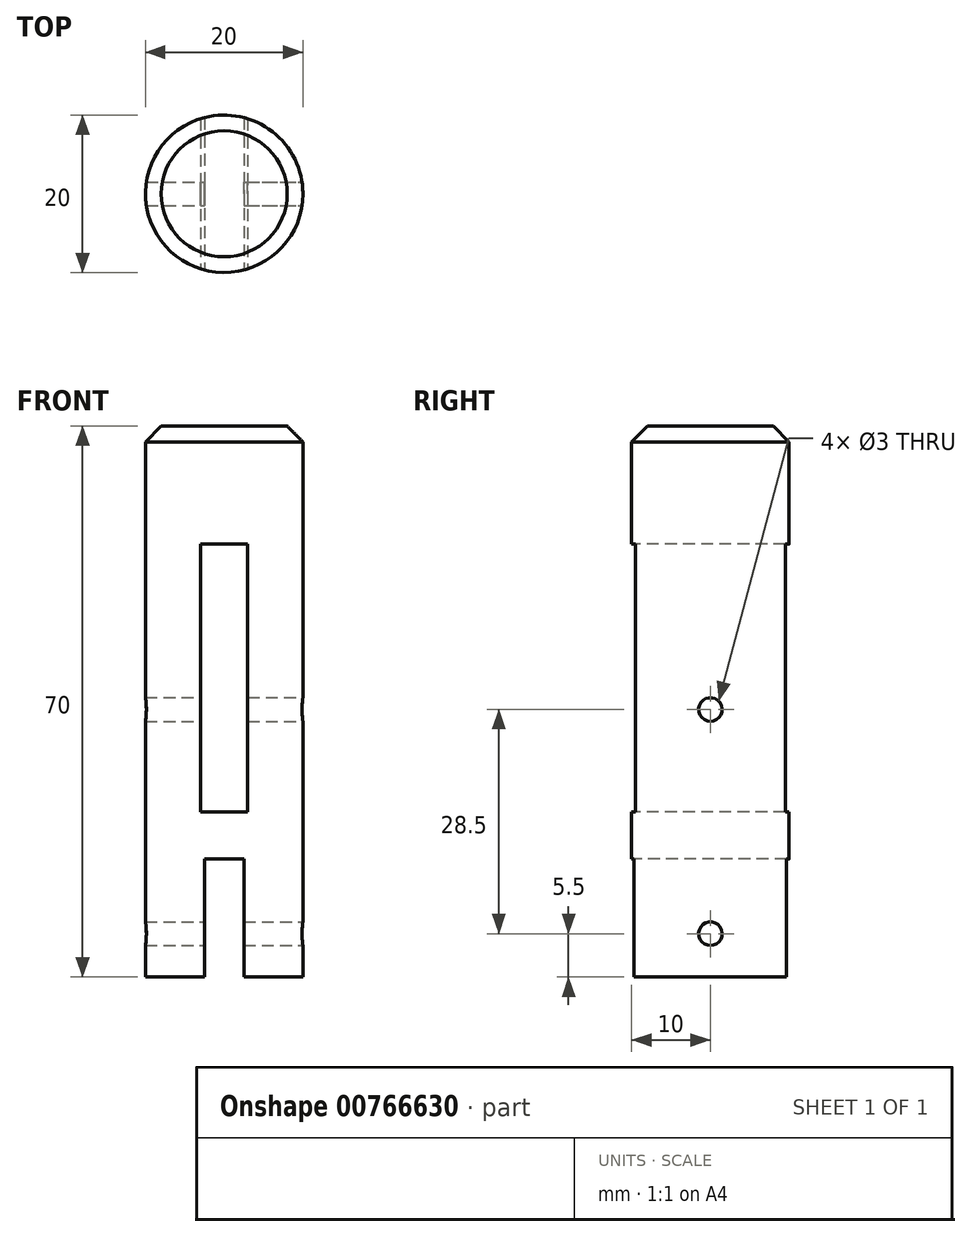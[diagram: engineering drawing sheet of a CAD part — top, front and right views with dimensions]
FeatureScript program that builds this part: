
annotation { "Feature Type Name" : "Feature", "Feature Type Description" : "" }
export const myFeature = defineFeature(function(context is Context, id is Id, definition is map)
    precondition{}
    {
        {
            var Q0;
            Q0=qCreatedBy(makeId("Top.planeOp"),FACE);
            var sketch = newSketch(context, id + "F0", { "sketchPlane" : qUnion([Q0])});
            skCircle(sketch, "E0", {"center": v(0, 0) * mm, "radius": 10 * mm});
            skLineSegment(sketch, "E1", {"start": v(2.5, 9.68) * mm, "end": v(2.5, -9.68) * mm});
            skLineSegment(sketch, "E2", {"start": v(-2.5, 9.68) * mm, "end": v(-2.5, -9.68) * mm});
            skSolve(sketch);
        }
        {
            var Q0;
            Q0 = qSketchRegion(id + "F0", true);
            extrude(context, id + "F1", {"entities" : qUnion([Q0]), "depth" : 55 * mm, "offsetDistance" : 25 * mm});
        }
        {
            var Q0;
            {var subQ0=sQuery(id+"F0.wireOp",EDGE,"E2");Q0=makeQuery(id+"F0.imprint","IMPRINT",FACE,{"disambiguationData":[TD([[makeQuery(id+"F0.imprint","IMPRINT",EDGE,{"derivedFrom":subQ0}),-1.0]])]});}
            var Q1;
            {var subQ0=sQuery(id+"F0.wireOp",EDGE,"E1");Q1=makeQuery(id+"F0.imprint","IMPRINT",FACE,{"disambiguationData":[TD([[makeQuery(id+"F0.imprint","IMPRINT",EDGE,{"derivedFrom":subQ0}),1.0]])]});}
            extrude(context, id + "F2", {"entities" : qUnion([Q0, Q1]), "operationType" : NewBodyOperationType.ADD, "depth" : -15 * mm, "offsetDistance" : 25 * mm});
        }
        {
            var Q0;
            Q0=makeQuery(id+"F1.opExtrude","CAP_FACE",FACE,{"disambiguationData":[OSD([sQuery(id+"F0.wireOp",EDGE,"E0")])],"isStart":false});
            chamfer(context, id + "F3", {"entities" : qUnion([Q0]), "width" : 2 * mm, "tangentPropagation" : true});
        }
        {
            var Q0;
            Q0=qCreatedBy(makeId("Right.planeOp"),FACE);
            var sketch = newSketch(context, id + "F4", { "sketchPlane" : qUnion([Q0])});
            skCircle(sketch, "E3", {"center": v(0, -9.5) * mm, "radius": 1.5 * mm});
            skSolve(sketch);
        }
        {
            var Q0;
            Q0 = qSketchRegion(id + "F4", true);
            extrude(context, id + "F5", {"entities" : qUnion([Q0]), "operationType" : NewBodyOperationType.REMOVE, "endBound" : BoundingType.SYMMETRIC, "oppositeDirection" : true, "depth" : 50 * mm, "offsetDistance" : 25 * mm});
        }
        {
            var Q0;
            Q0=qCreatedBy(makeId("Front.planeOp"),FACE);
            var sketch = newSketch(context, id + "F6", { "sketchPlane" : qUnion([Q0])});
            skLineSegment(sketch, "E4.bottom", {"start": v(3, 40) * mm, "end": v(-3, 40) * mm});
            skLineSegment(sketch, "E4.top", {"start": v(3, 6) * mm, "end": v(-3, 6) * mm});
            skLineSegment(sketch, "E4.left", {"start": v(3, 40) * mm, "end": v(3, 6) * mm});
            skLineSegment(sketch, "E4.right", {"start": v(-3, 40) * mm, "end": v(-3, 6) * mm});
            skPoint(sketch, "E4.middle", {"position": v(0, 23) * mm});
            skSolve(sketch);
        }
        {
            var Q0;
            Q0 = qSketchRegion(id + "F6", true);
            extrude(context, id + "F7", {"entities" : qUnion([Q0]), "operationType" : NewBodyOperationType.REMOVE, "endBound" : BoundingType.SYMMETRIC, "oppositeDirection" : true, "depth" : 25 * mm, "offsetDistance" : 25 * mm});
        }
        {
            var Q0;
            Q0=qCreatedBy(makeId("Right.planeOp"),FACE);
            var sketch = newSketch(context, id + "F8", { "sketchPlane" : qUnion([Q0])});
            skCircle(sketch, "E5", {"center": v(0, 19) * mm, "radius": 1.5 * mm});
            skSolve(sketch);
        }
        {
            var Q0;
            Q0 = qSketchRegion(id + "F8", true);
            extrude(context, id + "F9", {"entities" : qUnion([Q0]), "operationType" : NewBodyOperationType.REMOVE, "endBound" : BoundingType.SYMMETRIC, "oppositeDirection" : true, "depth" : 25 * mm, "offsetDistance" : 25 * mm});
        }
    });
